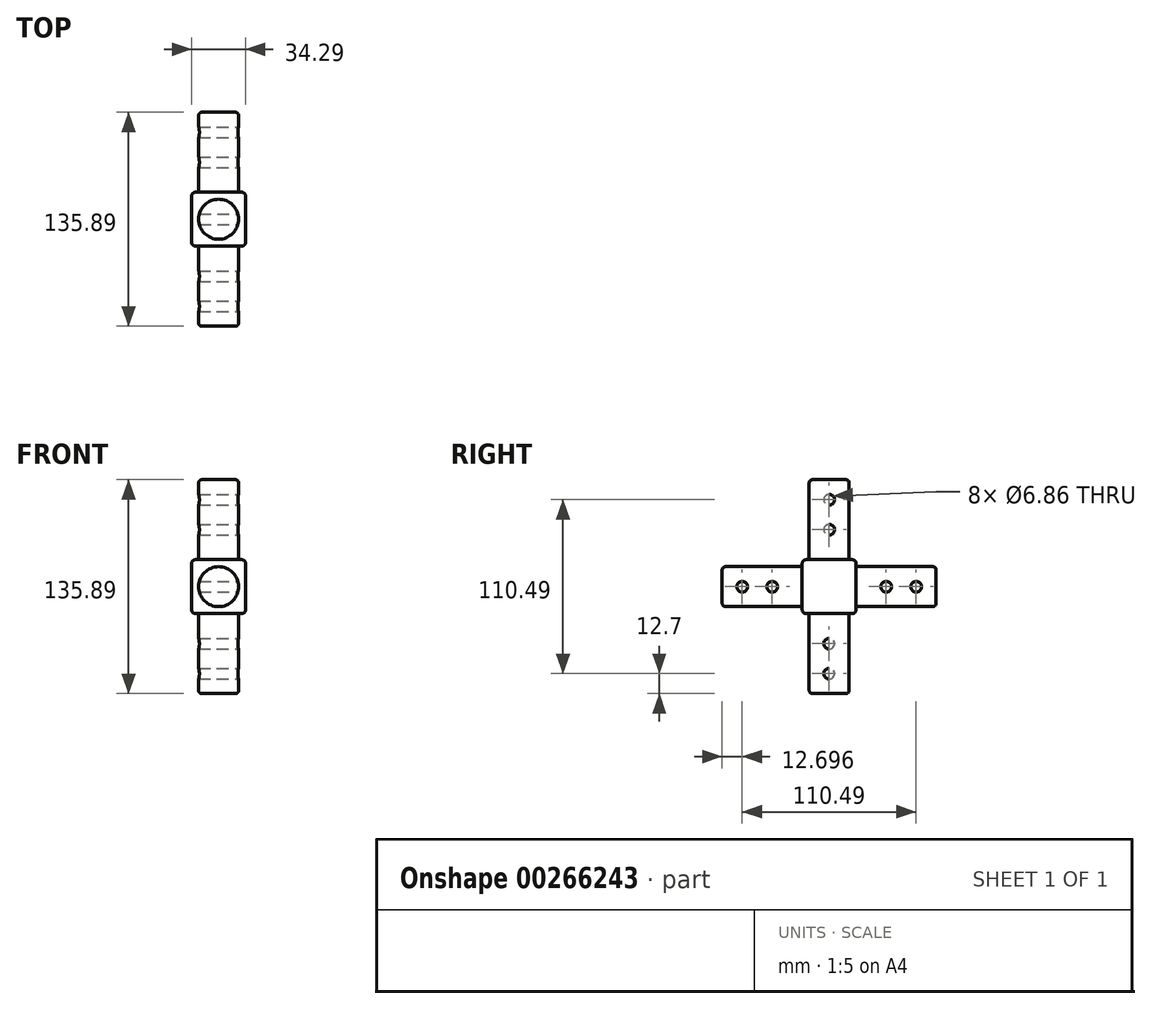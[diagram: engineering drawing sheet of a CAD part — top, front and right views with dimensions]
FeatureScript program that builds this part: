
annotation { "Feature Type Name" : "Feature", "Feature Type Description" : "" }
export const myFeature = defineFeature(function(context is Context, id is Id, definition is map)
    precondition{}
    {
        {
            var Q0;
            Q0=qCreatedBy(makeId("Top.planeOp"),FACE);
            var sketch = newSketch(context, id + "F0", { "sketchPlane" : qUnion([Q0])});
            skLineSegment(sketch, "E0.bottom", {"start": v(-13.47, 23.7) * mm, "end": v(20.82, 23.7) * mm});
            skLineSegment(sketch, "E0.top", {"start": v(-13.47, -10.58) * mm, "end": v(20.82, -10.58) * mm});
            skLineSegment(sketch, "E0.left", {"start": v(-13.47, 23.7) * mm, "end": v(-13.47, -10.58) * mm});
            skLineSegment(sketch, "E0.right", {"start": v(20.82, 23.7) * mm, "end": v(20.82, -10.58) * mm});
            skSolve(sketch);
        }
        {
            var Q0;
            Q0=qSketchRegion(id+"F0",true);
            extrude(context, id + "F1", {"entities" : qUnion([Q0]), "depth" : 34.3 * mm});
        }
        {
            var Q0;
            Q0=makeQuery(id+"F1.opExtrude","CAP_FACE",FACE,{"disambiguationData":[OSD([sQuery(id+"F0.wireOp",EDGE,"E0.bottom"),sQuery(id+"F0.wireOp",EDGE,"E0.top"),sQuery(id+"F0.wireOp",EDGE,"E0.left"),sQuery(id+"F0.wireOp",EDGE,"E0.right")])],"isStart":false});
            var sketch = newSketch(context, id + "F2", { "sketchPlane" : qUnion([Q0])});
            skCircle(sketch, "E1", {"center": v(3.68, 6.56) * mm, "radius": 12.7 * mm});
            skLineSegment(sketch, "E2", {"start": v(3.67, 23.7) * mm, "end": v(3.67, -12.79) * mm, "construction": true});
            skLineSegment(sketch, "E3", {"start": v(20.82, 6.56) * mm, "end": v(-13.47, 6.56) * mm, "construction": true});
            skSolve(sketch);
        }
        {
            var Q0;
            Q0=qSketchRegion(id+"F2",true);
            extrude(context, id + "F3", {"entities" : qUnion([Q0]), "operationType" : NewBodyOperationType.ADD, "depth" : 50.8 * mm});
        }
        {
            var Q0;
            Q0=makeQuery(id+"F1.opExtrude","SWEPT_FACE",FACE,{"disambiguationData":[OSD([sQuery(id+"F0.wireOp",EDGE,"E0.top")])]});
            var sketch = newSketch(context, id + "F4", { "sketchPlane" : qUnion([Q0])});
            skLineSegment(sketch, "E4", {"start": v(-13.47, 17.15) * mm, "end": v(24.43, 17.15) * mm, "construction": true});
            skLineSegment(sketch, "E5", {"start": v(3.67, 0) * mm, "end": v(3.67, 34.3) * mm, "construction": true});
            skCircle(sketch, "E6", {"center": v(3.67, 17.15) * mm, "radius": 12.7 * mm});
            skSolve(sketch);
        }
        {
            var Q0;
            Q0=qSketchRegion(id+"F4",true);
            extrude(context, id + "F5", {"entities" : qUnion([Q0]), "operationType" : NewBodyOperationType.ADD, "depth" : 50.8 * mm});
        }
        {
            var Q0;
            Q0=qCreatedBy(makeId("Right.planeOp"),FACE);
            var sketch = newSketch(context, id + "F6", { "sketchPlane" : qUnion([Q0])});
            skCircle(sketch, "E7", {"center": v(6.56, 53.34) * mm, "radius": 3.43 * mm});
            skCircle(sketch, "E8", {"center": v(6.56, 72.4) * mm, "radius": 3.43 * mm});
            skSolve(sketch);
        }
        {
            var Q0;
            Q0=qSketchRegion(id+"F6",true);
            extrude(context, id + "F7", {"entities" : qUnion([Q0]), "operationType" : NewBodyOperationType.REMOVE, "endBound" : BoundingType.SYMMETRIC, "oppositeDirection" : true, "depth" : 50.8 * mm});
        }
        {
            var Q0;
            Q0=qCreatedBy(makeId("Right.planeOp"),FACE);
            var sketch = newSketch(context, id + "F8", { "sketchPlane" : qUnion([Q0])});
            skCircle(sketch, "E9", {"center": v(-29.63, 17.15) * mm, "radius": 3.43 * mm});
            skCircle(sketch, "E10", {"center": v(-48.68, 17.15) * mm, "radius": 3.43 * mm});
            skSolve(sketch);
        }
        {
            var Q0;
            Q0=qSketchRegion(id+"F8",true);
            extrude(context, id + "F9", {"entities" : qUnion([Q0]), "operationType" : NewBodyOperationType.REMOVE, "endBound" : BoundingType.SYMMETRIC, "oppositeDirection" : true, "depth" : 50.8 * mm});
        }
        {
            var Q0;
            Q0=qCreatedBy(makeId("Front.planeOp"),FACE);
            var sketch = newSketch(context, id + "F10", { "sketchPlane" : qUnion([Q0])});
            skCircle(sketch, "E11", {"center": v(-51.57, 17.15) * mm, "radius": 3.43 * mm});
            skCircle(sketch, "E12", {"center": v(-32.52, 17.15) * mm, "radius": 3.43 * mm});
            skSolve(sketch);
        }
        {
            var Q0;
            Q0=qSketchRegion(id+"F10",true);
            extrude(context, id + "F11", {"entities" : qUnion([Q0]), "operationType" : NewBodyOperationType.REMOVE, "endBound" : BoundingType.SYMMETRIC, "oppositeDirection" : true, "depth" : 50.8 * mm});
        }
        {
            var Q0;
            Q0=makeQuery(id+"F1.opExtrude","SWEPT_EDGE",EDGE,{"disambiguationData":[OSD([sQuery(id+"F0.wireOp",EDGE,"E0.bottom"),sQuery(id+"F0.wireOp",EDGE,"E0.right")])]});
            var Q1;
            Q1=makeQuery(id+"F1.opExtrude","CAP_EDGE",EDGE,{"disambiguationData":[OSD([sQuery(id+"F0.wireOp",EDGE,"E0.right")])],"isStart":false});
            var Q2;
            Q2=makeQuery(id+"F1.opExtrude","SWEPT_EDGE",EDGE,{"disambiguationData":[OSD([sQuery(id+"F0.wireOp",EDGE,"E0.top"),sQuery(id+"F0.wireOp",EDGE,"E0.right")])]});
            var Q3;
            Q3=makeQuery(id+"F1.opExtrude","CAP_EDGE",EDGE,{"disambiguationData":[OSD([sQuery(id+"F0.wireOp",EDGE,"E0.right")])],"isStart":true});
            var Q4;
            Q4=makeQuery(id+"F1.opExtrude","CAP_EDGE",EDGE,{"disambiguationData":[OSD([sQuery(id+"F0.wireOp",EDGE,"E0.bottom")])],"isStart":true});
            var Q5;
            Q5=makeQuery(id+"F1.opExtrude","CAP_EDGE",EDGE,{"disambiguationData":[OSD([sQuery(id+"F0.wireOp",EDGE,"E0.bottom")])],"isStart":false});
            var Q6;
            Q6=makeQuery(id+"F1.opExtrude","SWEPT_EDGE",EDGE,{"disambiguationData":[OSD([sQuery(id+"F0.wireOp",EDGE,"E0.bottom"),sQuery(id+"F0.wireOp",EDGE,"E0.left")])]});
            var Q7;
            Q7=makeQuery(id+"F1.opExtrude","CAP_EDGE",EDGE,{"disambiguationData":[OSD([sQuery(id+"F0.wireOp",EDGE,"E0.left")])],"isStart":true});
            var Q8;
            Q8=makeQuery(id+"F1.opExtrude","CAP_EDGE",EDGE,{"disambiguationData":[OSD([sQuery(id+"F0.wireOp",EDGE,"E0.top")])],"isStart":true});
            var Q9;
            Q9=makeQuery(id+"F1.opExtrude","CAP_EDGE",EDGE,{"disambiguationData":[OSD([sQuery(id+"F0.wireOp",EDGE,"E0.left")])],"isStart":false});
            var Q10;
            Q10=makeQuery(id+"F1.opExtrude","SWEPT_EDGE",EDGE,{"disambiguationData":[OSD([sQuery(id+"F0.wireOp",EDGE,"E0.top"),sQuery(id+"F0.wireOp",EDGE,"E0.left")])]});
            var Q11;
            Q11=makeQuery(id+"F1.opExtrude","CAP_EDGE",EDGE,{"disambiguationData":[OSD([sQuery(id+"F0.wireOp",EDGE,"E0.top")])],"isStart":false});
            fillet(context, id + "F12", {"entities" : qUnion([Q0, Q1, Q2, Q3, Q4, Q5, Q6, Q7, Q8, Q9, Q10, Q11]), "radius" : 2.54 * mm, "tangentPropagation" : true, "allowEdgeOverflow" : false});
        }
        {
            var Q0;
            Q0=makeQuery(id+"F1.opExtrude","SWEPT_FACE",FACE,{"disambiguationData":[OSD([sQuery(id+"F0.wireOp",EDGE,"E0.bottom")])]});
            var sketch = newSketch(context, id + "F13", { "sketchPlane" : qUnion([Q0])});
            skLineSegment(sketch, "E13", {"start": v(-18.28, 17.15) * mm, "end": v(4.82, 17.15) * mm, "construction": true});
            skPoint(sketch, "E13.endSnap0", {"position": v(-18.28, 17.15) * mm});
            skLineSegment(sketch, "E14", {"start": v(-3.67, 31.75) * mm, "end": v(-3.67, 14.65) * mm, "construction": true});
            skCircle(sketch, "E15", {"center": v(-3.67, 17.15) * mm, "radius": 12.7 * mm});
            skSolve(sketch);
        }
        {
            var Q0;
            Q0=qSketchRegion(id+"F13",true);
            extrude(context, id + "F14", {"entities" : qUnion([Q0]), "operationType" : NewBodyOperationType.ADD, "depth" : 50.8 * mm});
        }
        {
            var Q0;
            Q0=qCreatedBy(makeId("Right.planeOp"),FACE);
            var sketch = newSketch(context, id + "F15", { "sketchPlane" : qUnion([Q0])});
            skCircle(sketch, "E16", {"center": v(42.76, 17.15) * mm, "radius": 3.43 * mm});
            skCircle(sketch, "E17", {"center": v(61.8, 17.15) * mm, "radius": 3.43 * mm});
            skSolve(sketch);
        }
        {
            var Q0;
            Q0=qSketchRegion(id+"F15",true);
            extrude(context, id + "F16", {"entities" : qUnion([Q0]), "operationType" : NewBodyOperationType.REMOVE, "endBound" : BoundingType.SYMMETRIC, "oppositeDirection" : true, "depth" : 50.8 * mm});
        }
        {
            var Q0;
            Q0=qCreatedBy(makeId("Front.planeOp"),FACE);
            var sketch = newSketch(context, id + "F17", { "sketchPlane" : qUnion([Q0])});
            skCircle(sketch, "E18", {"center": v(58.92, 17.15) * mm, "radius": 3.43 * mm});
            skCircle(sketch, "E19", {"center": v(39.87, 17.15) * mm, "radius": 3.43 * mm});
            skSolve(sketch);
        }
        {
            var Q0;
            Q0=qSketchRegion(id+"F17",true);
            extrude(context, id + "F18", {"entities" : qUnion([Q0]), "operationType" : NewBodyOperationType.REMOVE, "endBound" : BoundingType.SYMMETRIC, "oppositeDirection" : true, "depth" : 50.8 * mm});
        }
        {
            var Q0;
            Q0=makeQuery(id+"F1.opExtrude","CAP_FACE",FACE,{"disambiguationData":[OSD([sQuery(id+"F0.wireOp",EDGE,"E0.bottom"),sQuery(id+"F0.wireOp",EDGE,"E0.top"),sQuery(id+"F0.wireOp",EDGE,"E0.left"),sQuery(id+"F0.wireOp",EDGE,"E0.right")])],"isStart":true});
            var sketch = newSketch(context, id + "F19", { "sketchPlane" : qUnion([Q0])});
            skCircle(sketch, "E20", {"center": v(3.67, -6.56) * mm, "radius": 12.7 * mm});
            skPoint(sketch, "E20.centerSnap0", {"position": v(3.67, -21.17) * mm});
            skPoint(sketch, "E20.centerSnap1", {"position": v(-10.93, -6.56) * mm});
            skSolve(sketch);
        }
        {
            var Q0;
            Q0=qSketchRegion(id+"F19",true);
            extrude(context, id + "F20", {"entities" : qUnion([Q0]), "operationType" : NewBodyOperationType.ADD, "depth" : 50.8 * mm});
        }
        {
            var Q0;
            Q0=qCreatedBy(makeId("Right.planeOp"),FACE);
            var sketch = newSketch(context, id + "F21", { "sketchPlane" : qUnion([Q0])});
            skCircle(sketch, "E21", {"center": v(6.56, -19.05) * mm, "radius": 3.43 * mm});
            skCircle(sketch, "E22", {"center": v(6.56, -38.1) * mm, "radius": 3.43 * mm});
            skSolve(sketch);
        }
        {
            var Q0;
            Q0=qSketchRegion(id+"F21",true);
            extrude(context, id + "F22", {"entities" : qUnion([Q0]), "operationType" : NewBodyOperationType.REMOVE, "endBound" : BoundingType.SYMMETRIC, "oppositeDirection" : true, "depth" : 50.8 * mm});
        }
        {
            var Q0;
            Q0=makeQuery(id+"F3.opExtrude","CAP_EDGE",EDGE,{"disambiguationData":[OSD([sQuery(id+"F2.wireOp",EDGE,"E1")])],"isStart":false});
            var Q1;
            Q1=makeQuery(id+"F5.opExtrude","CAP_EDGE",EDGE,{"disambiguationData":[OSD([sQuery(id+"F4.wireOp",EDGE,"E6")])],"isStart":false});
            var Q2;
            Q2=makeQuery(id+"FYh3p2H8bsy1Prt_1.opExtrude","CAP_EDGE",EDGE,{"disambiguationData":[OSD([sQuery(id+"FIc3ZwD0MRkNizU_1.wireOp",EDGE,"5X2wenA0-NZPo-tNKO-rhVc-4ux0vwX6K1N9")])],"isStart":false});
            var Q3;
            Q3=makeQuery(id+"F14.opExtrude","CAP_EDGE",EDGE,{"disambiguationData":[OSD([sQuery(id+"F13.wireOp",EDGE,"E15")])],"isStart":false});
            var Q4;
            Q4=makeQuery(id+"F9gDW6ytOR0zG9s_1.opExtrude","CAP_EDGE",EDGE,{"disambiguationData":[OSD([sQuery(id+"FiyRrB6nUQmxvW3_1.wireOp",EDGE,"TDc28uEK-sT7R-I2aJ-wYcu-fXwbEVHNaGzo")])],"isStart":false});
            var Q5;
            Q5=makeQuery(id+"F20.opExtrude","CAP_EDGE",EDGE,{"disambiguationData":[OSD([sQuery(id+"F19.wireOp",EDGE,"E20")])],"isStart":false});
            fillet(context, id + "F23", {"entities" : qUnion([Q0, Q1, Q2, Q3, Q4, Q5]), "radius" : 2.03 * mm, "tangentPropagation" : true, "allowEdgeOverflow" : false});
        }
    });
